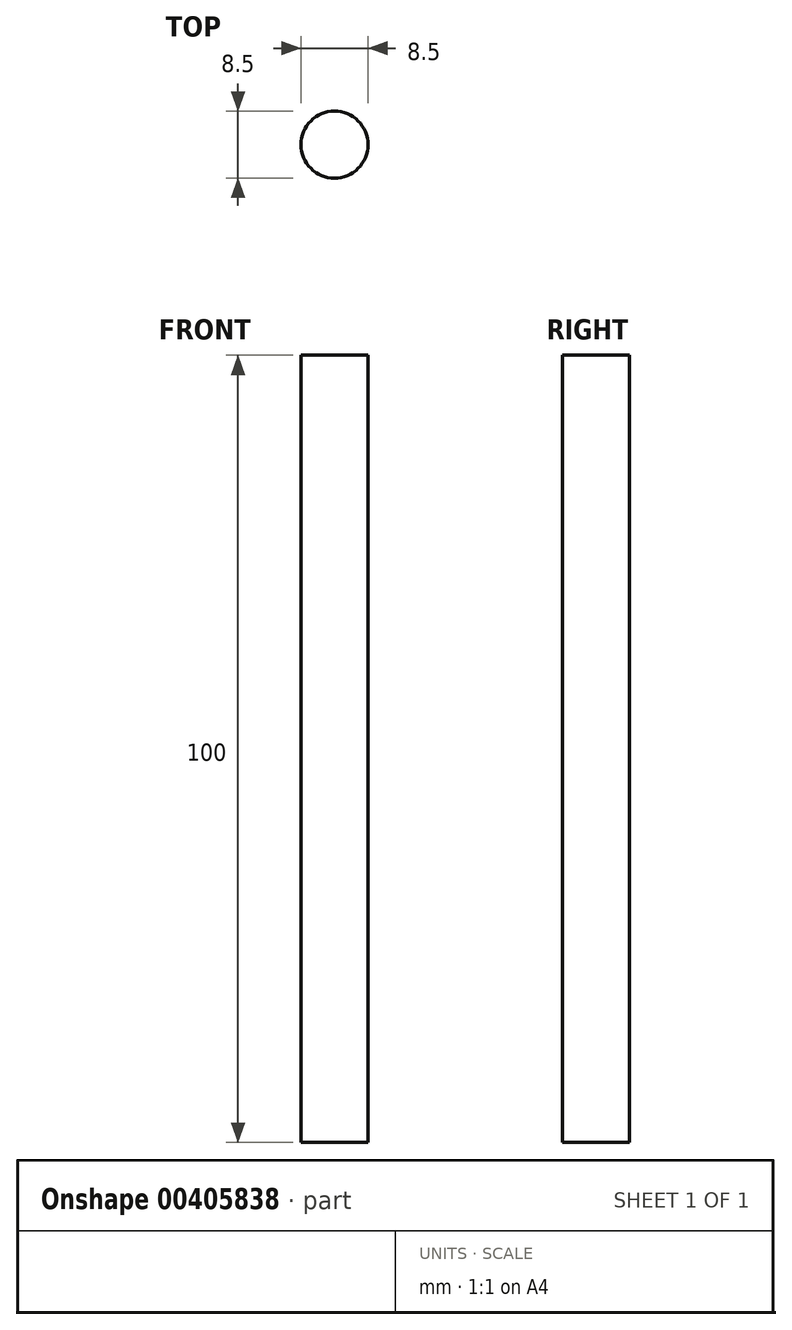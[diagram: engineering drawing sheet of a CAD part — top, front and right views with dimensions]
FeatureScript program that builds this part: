
annotation { "Feature Type Name" : "Feature", "Feature Type Description" : "" }
export const myFeature = defineFeature(function(context is Context, id is Id, definition is map)
    precondition{}
    {
        {
            var Q0;
            Q0=qCreatedBy(makeId("Top.planeOp"),FACE);
            var sketch = newSketch(context, id + "F0", { "sketchPlane" : qUnion([Q0])});
            skCircle(sketch, "E0", {"center": v(0, 0) * mm, "radius": 4.25 * mm});
            skSolve(sketch);
        }
        {
            var Q0;
            Q0=makeQuery(id+"F0.imprint","IMPRINT",FACE,{"disambiguationData":[TD([[makeQuery(id+"F0.imprint","IMPRINT",EDGE,{"derivedFrom":sQuery(id+"F0.wireOp",EDGE,"E0")}),1.0]])]});
            extrude(context, id + "F1", {"entities" : qUnion([Q0]), "endBound" : BoundingType.SYMMETRIC, "depth" : 100 * mm});
        }
    });
